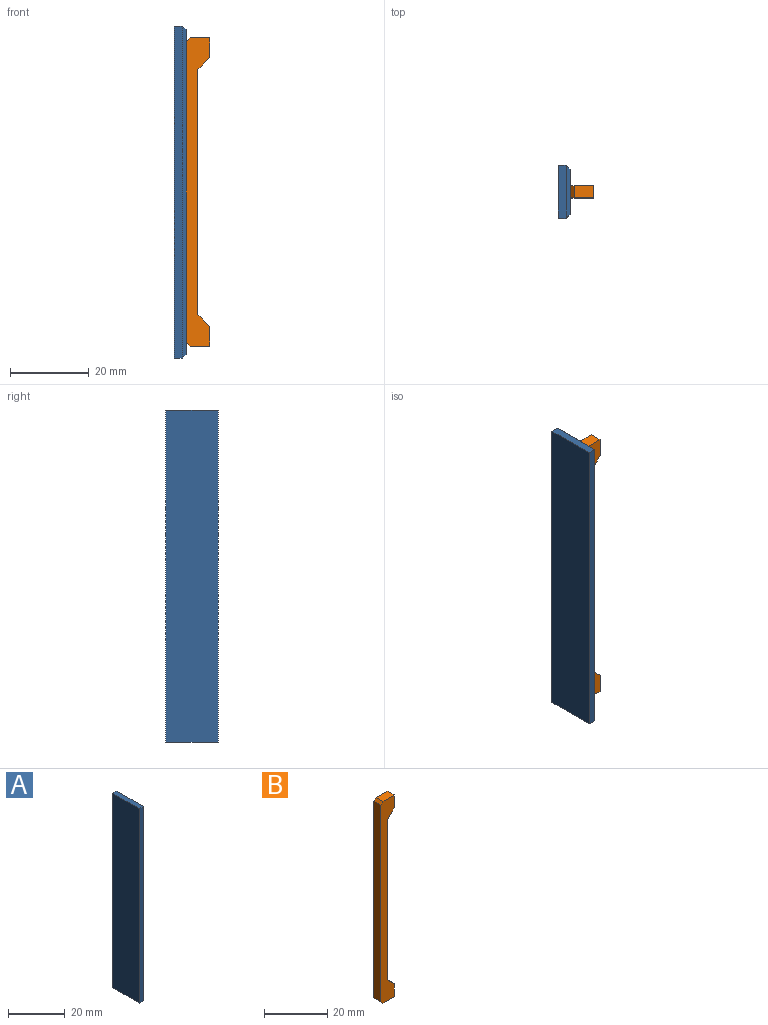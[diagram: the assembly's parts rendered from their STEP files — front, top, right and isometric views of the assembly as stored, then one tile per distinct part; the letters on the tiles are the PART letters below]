
ASSEMBLY  parts=2 mates=1
PART A: 15 faces, bbox 3x13.4x84.2 mm
  f0: plane 84.2x2mm, normal (0,1,0), area 168.4mm2, adj f1,f3,f4,f11
  f1: plane 13.4x2mm, normal (0,0,1), area 26.8mm2, adj f0,f2,f4,f13
  f2: plane 84.2x2mm, normal (0,-1,0), area 168.4mm2, adj f1,f3,f4,f14
  f3: plane 13.4x2mm, normal (0,0,-1), area 26.8mm2, adj f0,f2,f4,f12
  f4: plane 84.2x13.4mm, normal (-1,0,0), area 1128.3mm2, adj f0,f1,f2,f3
  f5: plane 3.4x2mm, normal (0,0,-1), area 6.8mm2, adj f6,f8,f9,f10
  f6: plane 78.2x2mm, normal (0,-1,0), area 156.4mm2, adj f5,f7,f9,f10
  f7: plane 3.4x2mm, normal (0,0,1), area 6.8mm2, adj f6,f8,f9,f10
  f8: plane 78.2x2mm, normal (0,1,0), area 156.4mm2, adj f5,f7,f9,f10
  f9: plane 82.2x11.4mm, normal (1,0,0), area 671.2mm2, adj f5,f6,f7,f8,f11,f12,f13,f14
  f10: plane 78.2x3.4mm, normal (1,0,0), area 265.9mm2, adj f5,f6,f7,f8
  f11: plane 84.2x1mm, normal (0.71,0.71,0), area 117.7mm2, adj f0,f9,f12,f13
  f12: plane 13.4x1mm, normal (0.71,0,-0.71), area 17.5mm2, adj f3,f9,f11,f14
  f13: plane 13.4x1mm, normal (0.71,0,0.71), area 17.5mm2, adj f1,f9,f11,f14
  f14: plane 84.2x1mm, normal (0.71,-0.71,0), area 117.7mm2, adj f2,f9,f12,f13
PART B: 20 faces, bbox 6x3.1x78.2 mm
  f0: plane 76.2x1.5mm, normal (1,0,0), area 114.3mm2, adj f2,f5,f8,f11
  f1: plane 76.2x3.1mm, normal (-1,0,0), area 236.2mm2, adj f3,f6,f14,f15
  f2: plane 76.2x5mm, normal (0,1,0), area 185.4mm2, adj f0,f4,f8,f10,f11,f13,f17,f19
  f3: plane 78.2x6mm, normal (0,-1,0), area 272.6mm2, adj f1,f4,f9,f10,f12,f13,f14,f15
  f4: plane 62.2x0.8mm, normal (1,0,0), area 49.8mm2, adj f2,f3,f17,f19
  f5: plane 76.2x5mm, normal (0,-1,0), area 185.4mm2, adj f0,f7,f8,f10,f11,f13,f16,f18
  f6: plane 78.2x6mm, normal (0,1,0), area 272.6mm2, adj f1,f7,f9,f10,f12,f13,f14,f15
  f7: plane 62.2x0.8mm, normal (1,0,0), area 49.8mm2, adj f5,f6,f16,f18
  f8: plane 5x1.5mm, normal (0,0,-1), area 7.5mm2, adj f0,f2,f5,f10
  f9: plane 5x3.1mm, normal (0,0,1), area 15.5mm2, adj f3,f6,f10,f14
  f10: plane 5x3.1mm, normal (1,0,0), area 9.5mm2, adj f2,f3,f5,f6,f8,f9,f18,f19
  f11: plane 5x1.5mm, normal (0,0,1), area 7.5mm2, adj f0,f2,f5,f13
  f12: plane 5x3.1mm, normal (0,0,-1), area 15.5mm2, adj f3,f6,f13,f15
  f13: plane 5x3.1mm, normal (1,0,0), area 9.5mm2, adj f2,f3,f5,f6,f11,f12,f16,f17
  f14: plane 3.1x1mm, normal (-0.71,0,0.71), area 4.4mm2, adj f1,f3,f6,f9
  f15: plane 3.1x1mm, normal (-0.71,0,-0.71), area 4.4mm2, adj f1,f3,f6,f12
  f16: plane 3x3mm, normal (0.71,0,0.71), area 3.4mm2, adj f5,f6,f7,f13
  f17: plane 3x3mm, normal (0.71,0,0.71), area 3.4mm2, adj f2,f3,f4,f13
  f18: plane 3x3mm, normal (0.71,0,-0.71), area 3.4mm2, adj f5,f6,f7,f10
  f19: plane 3x3mm, normal (0.71,0,-0.71), area 3.4mm2, adj f2,f3,f4,f10
PLACE A t=(-14.89,31.81,-10.82)mm
PLACE B t=(-11.89,53.06,-12.82)mm
MATE fastened B.f1 <-> A.f9  axis (-1,0,0) through (-11.89,14.64,21.08)mm
